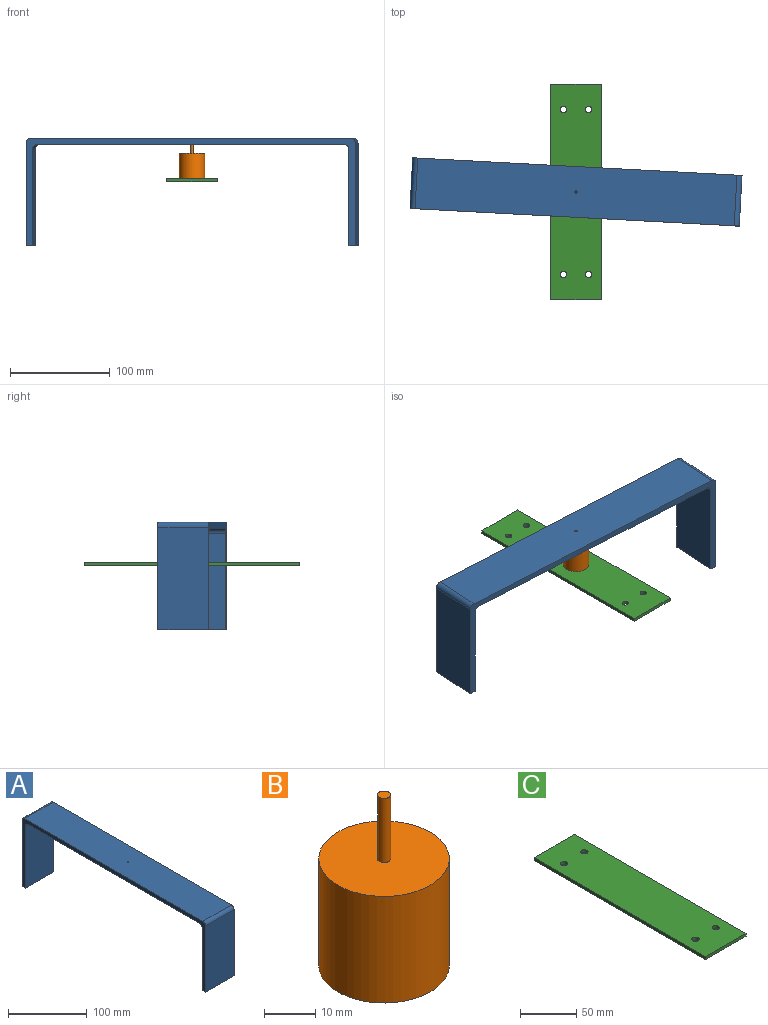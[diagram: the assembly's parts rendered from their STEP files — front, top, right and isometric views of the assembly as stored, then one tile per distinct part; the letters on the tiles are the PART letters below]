
ASSEMBLY  parts=3 mates=2
PART A: 15 faces, bbox 50.8x330.2x108 mm
  f0: plane 307.34x50.8mm, normal (0,0,-1), area 15607.8mm2, adj f2,f4,f5,f13,f14
  f1: plane 102.87x50.8mm, normal (0,-1,0), area 5225.8mm2, adj f2,f5,f8,f12
  f2: plane 330.2x107.95mm, normal (1,0,0), area 3387.1mm2, adj f0,f1,f3,f6,f7,f8,f9,f10
  f3: plane 102.87x50.8mm, normal (0,1,0), area 5225.8mm2, adj f2,f5,f10,f11
  f4: cylinder r=1.27mm len=6.35mm, axis (0,0,-1), area 50.7mm2, adj f0,f6
  f5: plane 330.2x107.95mm, normal (-1,0,0), area 3387.1mm2, adj f0,f1,f3,f6,f7,f8,f9,f10
  f6: plane 320.04x50.8mm, normal (0,0,1), area 16253mm2, adj f2,f4,f5,f11,f12
  f7: plane 96.52x50.8mm, normal (0,1,0), area 4903.2mm2, adj f2,f5,f8,f14
  f8: plane 50.8x6.35mm, normal (0,0,-1), area 322.6mm2, adj f1,f2,f5,f7
  f9: plane 96.52x50.8mm, normal (0,-1,0), area 4903.2mm2, adj f2,f5,f10,f13
  f10: plane 50.8x6.35mm, normal (0,0,-1), area 322.6mm2, adj f2,f3,f5,f9
  f11: cylinder r=5.08mm len=50.8mm, axis (1,0,0), area 405.4mm2, adj f2,f3,f5,f6
  f12: cylinder r=5.08mm len=50.8mm, axis (-1,0,0), area 405.4mm2, adj f1,f2,f5,f6
  f13: cylinder r=5.08mm len=50.8mm, axis (1,0,0), area 405.4mm2, adj f0,f2,f5,f9
  f14: cylinder r=5.08mm len=50.8mm, axis (-1,0,0), area 405.4mm2, adj f0,f2,f5,f7
PART B: 5 faces, bbox 25.4x25.4x40.6 mm
  f0: cylinder r=12.7mm len=25.4mm, axis (0,0,-1), area 2026.8mm2, adj f1,f2
  f1: plane 25.4x25.4mm, normal (0,0,1), area 501.6mm2, adj f0,f3
  f2: plane 25.4x25.4mm, normal (0,0,-1), area 506.7mm2, adj f0
  f3: cylinder r=1.27mm len=15.24mm, axis (0,0,-1), area 121.6mm2, adj f1,f4
  f4: plane 2.54x2.54mm, normal (0,0,1), area 5.1mm2, adj f3
PART C: 10 faces, bbox 50.8x215.9x3.2 mm
  f0: plane 50.8x3.18mm, normal (0,1,0), area 161.3mm2, adj f1,f7,f8,f9
  f1: plane 215.9x3.18mm, normal (-1,0,0), area 685.5mm2, adj f0,f2,f8,f9
  f2: plane 50.8x3.18mm, normal (0,-1,0), area 161.3mm2, adj f1,f7,f8,f9
  f3: cylinder r=3.17mm len=6.35mm, axis (0,0,-1), area 63.3mm2, adj f8,f9
  f4: cylinder r=3.17mm len=6.35mm, axis (0,0,-1), area 63.3mm2, adj f8,f9
  f5: cylinder r=3.17mm len=6.35mm, axis (0,0,-1), area 63.3mm2, adj f8,f9
  f6: cylinder r=3.17mm len=6.35mm, axis (0,0,-1), area 63.3mm2, adj f8,f9
  f7: plane 215.9x3.18mm, normal (1,0,0), area 685.5mm2, adj f0,f2,f8,f9
  f8: plane 215.9x50.8mm, normal (0,0,1), area 10841mm2, adj f0,f1,f2,f3,f4,f5,f6,f7
  f9: plane 215.9x50.8mm, normal (0,0,-1), area 10841mm2, adj f0,f1,f2,f3,f4,f5,f6,f7
PLACE A rot(axis=(0,0,1),86.9deg) t=(0,0,34.29)mm
PLACE B at identity
PLACE C t=(0,0,-3.17)mm fixed
MATE fastened C.f8 <-> B.f0  axis (0,0,1) through (0,0,0)mm
MATE revolute B.f3 <-> A.f4  axis (0,0,1) through (0,0,40.64)mm
